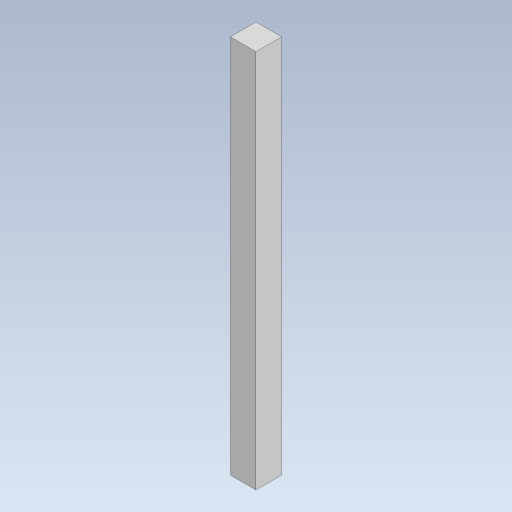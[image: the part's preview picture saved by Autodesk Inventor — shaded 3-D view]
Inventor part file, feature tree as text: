
AUTODESK INVENTOR PART (.ipt)
format: ipt  version: 2023 (Build 270158000, 158)  size: 240,128 bytes
history: native  units: in
note: dims shown in document units (in); Inventor stores cm internally (conversion verified against a paired STEP export)
features: extrude x1, sketch x1
ambient origin geometry x8: Origin, YZ Plane, XZ Plane, XY Plane, X Axis, Y Axis, Z Axis, Center Point
bodies: Solid1 (feature_tree)
feature tree (2):
  extrude  "Extrusion1"  Depth=0.3937in
  sketch  "Sketch1"  dims[d0=0.3937in d1=0.3937in d2=5.8268in d3=0.0in]
